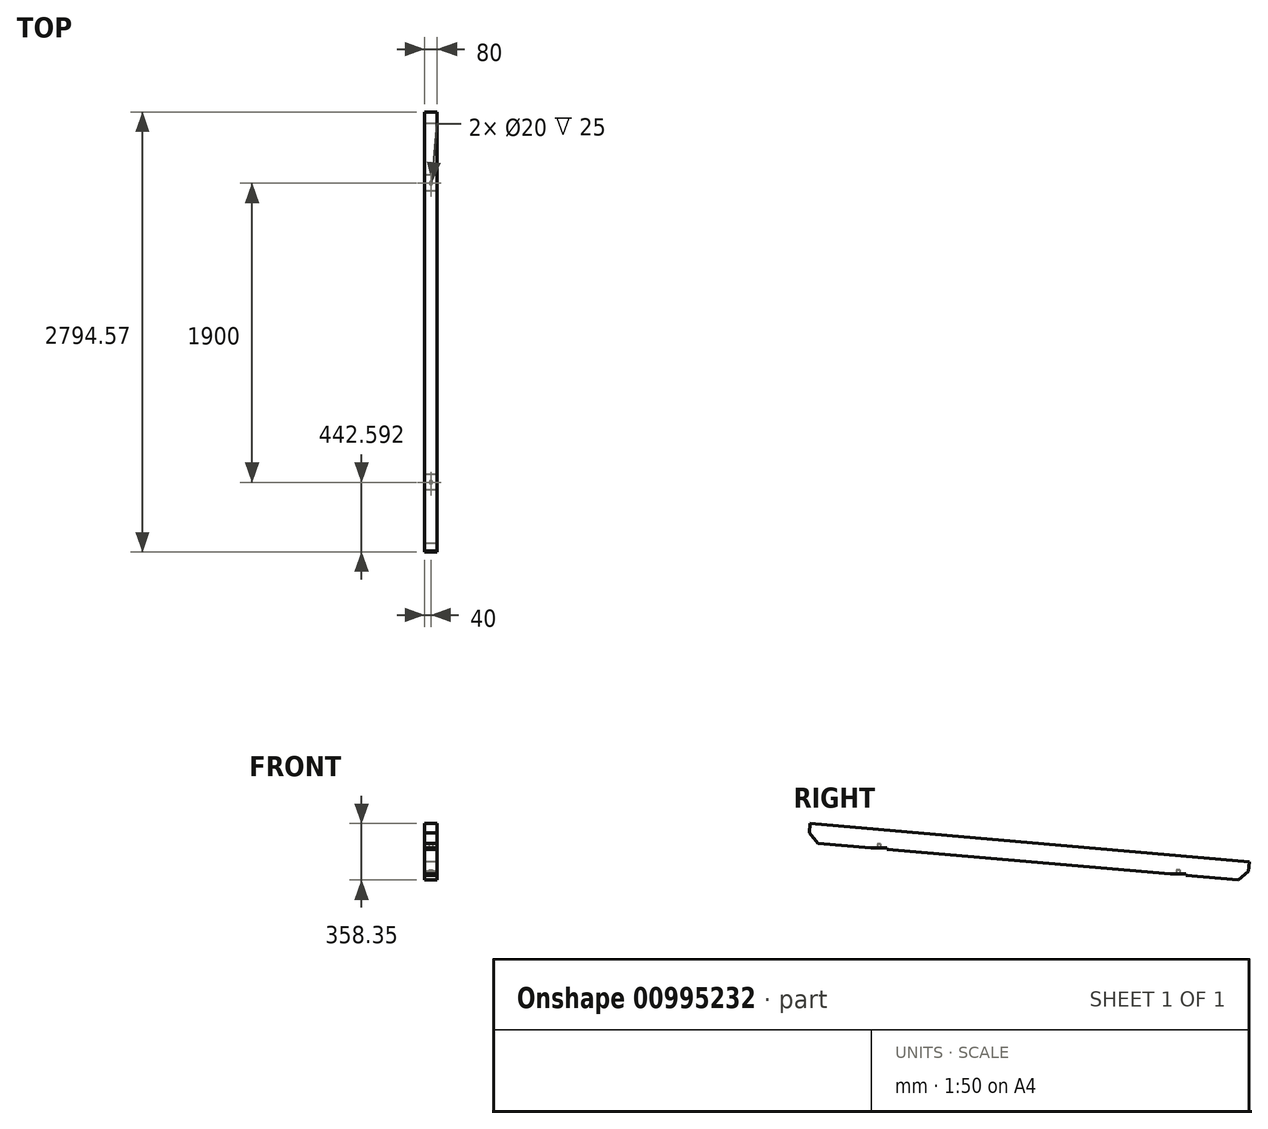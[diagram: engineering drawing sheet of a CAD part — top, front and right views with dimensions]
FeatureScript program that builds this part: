
annotation { "Feature Type Name" : "Feature", "Feature Type Description" : "" }
export const myFeature = defineFeature(function(context is Context, id is Id, definition is map)
    precondition{}
    {
        {
            var Q0;
            Q0=qCreatedBy(makeId("Right.planeOp"),FACE);
            var sketch = newSketch(context, id + "F0", { "sketchPlane" : qUnion([Q0])});
            skLineSegment(sketch, "E0.top", {"start": v(1789.3, -1187.3) * mm, "end": v(1889.3, -1187.3) * mm, "construction": true});
            skLineSegment(sketch, "E0.left", {"start": v(1789.3, 1112.7) * mm, "end": v(1789.3, -1187.3) * mm, "construction": true});
            skLineSegment(sketch, "E0.right", {"start": v(1889.3, 1103.95) * mm, "end": v(1889.3, -1187.3) * mm, "construction": true});
            skLineSegment(sketch, "E1", {"start": v(1399.3, -1187.3) * mm, "end": v(3873.55, -1187.3) * mm, "construction": true});
            skLineSegment(sketch, "E2.bottom", {"start": v(3689.3, -1187.3) * mm, "end": v(3789.3, -1187.3) * mm, "construction": true});
            skLineSegment(sketch, "E2.left", {"start": v(3689.3, -1187.3) * mm, "end": v(3689.3, 946.47) * mm, "construction": true});
            skLineSegment(sketch, "E2.right", {"start": v(3789.3, -1187.3) * mm, "end": v(3789.3, 937.72) * mm, "construction": true});
            skLineSegment(sketch, "E3.top", {"start": v(3789.3, 946.47) * mm, "end": v(3689.3, 946.47) * mm, "construction": true});
            skLineSegment(sketch, "E4.bottom", {"start": v(1401.93, 1267.04) * mm, "end": v(4191.27, 1023) * mm});
            skLineSegment(sketch, "E4.top", {"start": v(1391.47, 1147.5) * mm, "end": v(1789.3, 1112.7) * mm});
            skLineSegment(sketch, "E4.left", {"start": v(1401.93, 1267.04) * mm, "end": v(1391.47, 1147.5) * mm});
            skLineSegment(sketch, "E4.right", {"start": v(4191.27, 1023) * mm, "end": v(4180.82, 903.46) * mm});
            skLineSegment(sketch, "E5.trimOffspring", {"start": v(3789.3, 937.72) * mm, "end": v(4180.82, 903.46) * mm});
            skLineSegment(sketch, "E6.trimOffspring", {"start": v(1889.3, 1103.95) * mm, "end": v(3689.3, 946.47) * mm});
            skLineSegment(sketch, "E7", {"start": v(1239.32, 1267.04) * mm, "end": v(4403.4, 1267.04) * mm, "construction": true});
            skLineSegment(sketch, "E8", {"start": v(3689.3, 946.47) * mm, "end": v(3789.3, 946.47) * mm});
            skLineSegment(sketch, "E9", {"start": v(3789.3, 937.72) * mm, "end": v(3789.3, 946.47) * mm});
            skLineSegment(sketch, "E10", {"start": v(1789.3, 1112.7) * mm, "end": v(1889.3, 1112.7) * mm});
            skLineSegment(sketch, "E11", {"start": v(1889.3, 1112.7) * mm, "end": v(1889.3, 1103.95) * mm});
            skSolve(sketch);
        }
        {
            var Q0;
            Q0=makeQuery(id+"F0.imprint","IMPRINT",FACE,{"disambiguationData":[TD([[makeQuery(id+"F0.imprint","IMPRINT",EDGE,{"derivedFrom":sQuery(id+"F0.wireOp",EDGE,"E4.bottom")}),-1.0]])]});
            extrude(context, id + "F1", {"entities" : qUnion([Q0]), "depth" : 80 * mm, "offsetDistance" : 25 * mm});
        }
        {
            var Q0;
            Q0=makeQuery(id+"F1.opExtrude","SWEPT_EDGE",EDGE,{"disambiguationData":[OSD([sQuery(id+"F0.wireOp",EDGE,"E4.top"),sQuery(id+"F0.wireOp",EDGE,"E4.left")])]});
            var Q1;
            Q1=makeQuery(id+"F1.opExtrude","SWEPT_EDGE",EDGE,{"disambiguationData":[OSD([sQuery(id+"F0.wireOp",EDGE,"E4.right"),sQuery(id+"F0.wireOp",EDGE,"E5.trimOffspring")])]});
            chamfer(context, id + "F2", {"entities" : qUnion([Q0, Q1]), "width" : 60 * mm, "tangentPropagation" : true});
        }
        {
            var Q0;
            Q0=makeQuery(id+"F1.opExtrude","SWEPT_FACE",FACE,{"disambiguationData":[OSD([sQuery(id+"F0.wireOp",EDGE,"E10")])]});
            var sketch = newSketch(context, id + "F3", { "sketchPlane" : qUnion([Q0])});
            skCircle(sketch, "E12", {"center": v(40, -1839.3) * mm, "radius": 10 * mm});
            skPoint(sketch, "E12.centerSnap0", {"position": v(40, -1789.3) * mm});
            skPoint(sketch, "E12.centerSnap1", {"position": v(80, -1839.3) * mm});
            skSolve(sketch);
        }
        {
            var Q0;
            Q0=makeQuery(id+"F1.opExtrude","SWEPT_FACE",FACE,{"disambiguationData":[OSD([sQuery(id+"F0.wireOp",EDGE,"E8")])]});
            var sketch = newSketch(context, id + "F4", { "sketchPlane" : qUnion([Q0])});
            skCircle(sketch, "E13", {"center": v(40, -3739.3) * mm, "radius": 10 * mm});
            skPoint(sketch, "E13.centerSnap0", {"position": v(40, -3689.3) * mm});
            skPoint(sketch, "E13.centerSnap1", {"position": v(80, -3739.3) * mm});
            skSolve(sketch);
        }
        {
            var Q0;
            Q0=makeQuery(id+"F3.imprint","IMPRINT",FACE,{"disambiguationData":[TD([[makeQuery(id+"F3.imprint","IMPRINT",EDGE,{"derivedFrom":sQuery(id+"F3.wireOp",EDGE,"E12")}),1.0]])]});
            var Q1;
            Q1=makeQuery(id+"F4.imprint","IMPRINT",FACE,{"disambiguationData":[TD([[makeQuery(id+"F4.imprint","IMPRINT",EDGE,{"derivedFrom":sQuery(id+"F4.wireOp",EDGE,"E13")}),1.0]])]});
            extrude(context, id + "F5", {"entities" : qUnion([Q0, Q1]), "operationType" : NewBodyOperationType.REMOVE, "oppositeDirection" : true, "depth" : 25 * mm, "offsetDistance" : 25 * mm});
        }
    });
